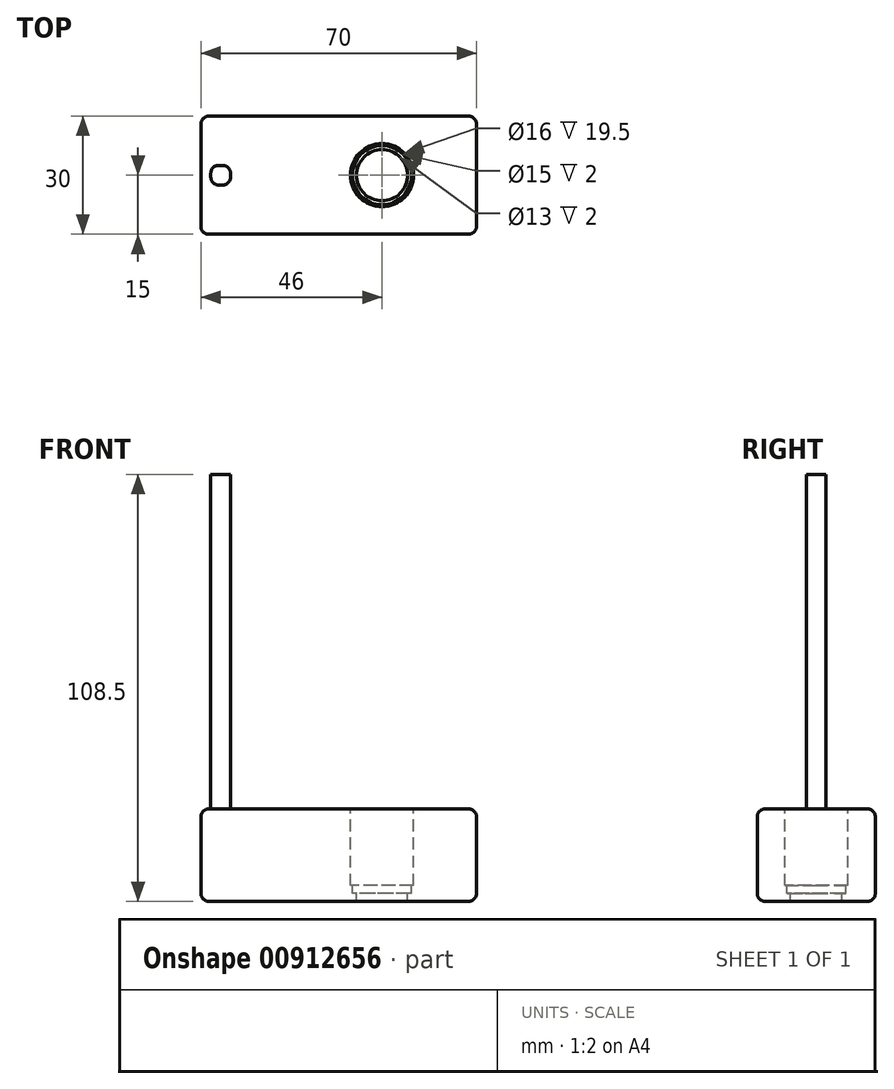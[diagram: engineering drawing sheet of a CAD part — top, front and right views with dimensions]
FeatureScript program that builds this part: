
annotation { "Feature Type Name" : "Feature", "Feature Type Description" : "" }
export const myFeature = defineFeature(function(context is Context, id is Id, definition is map)
    precondition{}
    {
        {
            var Q0;
            Q0=qCreatedBy(makeId("Front.planeOp"),FACE);
            var sketch = newSketch(context, id + "F0", { "sketchPlane" : qUnion([Q0])});
            skLineSegment(sketch, "E0.bottom", {"start": v(35, -11.75) * mm, "end": v(-35, -11.75) * mm});
            skLineSegment(sketch, "E0.top", {"start": v(35, 11.75) * mm, "end": v(-35, 11.75) * mm});
            skLineSegment(sketch, "E0.left", {"start": v(35, -11.75) * mm, "end": v(35, 11.75) * mm});
            skLineSegment(sketch, "E0.right", {"start": v(-35, -11.75) * mm, "end": v(-35, 11.75) * mm});
            skPoint(sketch, "E0.middle", {"position": v(0, 0) * mm});
            skSolve(sketch);
        }
        {
            var Q0;
            Q0=makeQuery(id+"F0.imprint","IMPRINT",FACE,{"disambiguationData":[TD([[makeQuery(id+"F0.imprint","IMPRINT",EDGE,{"derivedFrom":sQuery(id+"F0.wireOp",EDGE,"E0.bottom")}),-1.0]])]});
            extrude(context, id + "F1", {"entities" : qUnion([Q0]), "depth" : 30 * mm, "offsetDistance" : 25 * mm});
        }
        {
            var Q0;
            Q0=makeQuery(id+"F1.opExtrude","SWEPT_FACE",FACE,{"disambiguationData":[OSD([sQuery(id+"F0.wireOp",EDGE,"E0.top")])]});
            var sketch = newSketch(context, id + "F2", { "sketchPlane" : qUnion([Q0])});
            skLineSegment(sketch, "E1", {"start": v(35, -15) * mm, "end": v(11, -15) * mm, "construction": true});
            skCircle(sketch, "E2", {"center": v(11, -15) * mm, "radius": 8 * mm});
            skSolve(sketch);
        }
        {
            var Q0;
            Q0=makeQuery(id+"F2.imprint","IMPRINT",FACE,{"disambiguationData":[TD([[makeQuery(id+"F2.imprint","IMPRINT",EDGE,{"derivedFrom":sQuery(id+"F2.wireOp",EDGE,"E2")}),1.0]])]});
            extrude(context, id + "F3", {"entities" : qUnion([Q0]), "operationType" : NewBodyOperationType.REMOVE, "oppositeDirection" : true, "depth" : 19.5 * mm, "offsetDistance" : 25 * mm});
        }
        {
            var Q0;
            Q0=makeQuery(id+"F3.boolean.opBoolean","COPY",FACE,{"derivedFrom":makeQuery(id+"F3.opExtrude","CAP_FACE",FACE,{"disambiguationData":[OSD([sQuery(id+"F2.wireOp",EDGE,"E2")])],"isStart":false})});
            var sketch = newSketch(context, id + "F4", { "sketchPlane" : qUnion([Q0])});
            skCircle(sketch, "E3", {"center": v(11, -15) * mm, "radius": 7.5 * mm});
            skSolve(sketch);
        }
        {
            var Q0;
            Q0=makeQuery(id+"F4.imprint","IMPRINT",FACE,{"disambiguationData":[TD([[makeQuery(id+"F4.imprint","IMPRINT",EDGE,{"derivedFrom":sQuery(id+"F4.wireOp",EDGE,"E3")}),1.0]])]});
            extrude(context, id + "F5", {"entities" : qUnion([Q0]), "operationType" : NewBodyOperationType.REMOVE, "oppositeDirection" : true, "depth" : 2 * mm, "offsetDistance" : 25 * mm});
        }
        {
            var Q0;
            Q0=makeQuery(id+"F5.boolean.opBoolean","COPY",FACE,{"derivedFrom":makeQuery(id+"F5.opExtrude","CAP_FACE",FACE,{"disambiguationData":[OSD([sQuery(id+"F4.wireOp",EDGE,"E3")])],"isStart":false})});
            var sketch = newSketch(context, id + "F6", { "sketchPlane" : qUnion([Q0])});
            skCircle(sketch, "E4", {"center": v(11, -15) * mm, "radius": 6.5 * mm});
            skSolve(sketch);
        }
        {
            var Q0;
            Q0=makeQuery(id+"F6.imprint","IMPRINT",FACE,{"disambiguationData":[TD([[makeQuery(id+"F6.imprint","IMPRINT",EDGE,{"derivedFrom":sQuery(id+"F6.wireOp",EDGE,"E4")}),1.0]])]});
            extrude(context, id + "F7", {"entities" : qUnion([Q0]), "operationType" : NewBodyOperationType.REMOVE, "endBound" : BoundingType.THROUGH_ALL, "oppositeDirection" : true, "depth" : 25 * mm, "offsetDistance" : 25 * mm});
        }
        {
            var Q0;
            Q0=makeQuery(id+"F1.opExtrude","SWEPT_FACE",FACE,{"disambiguationData":[OSD([sQuery(id+"F0.wireOp",EDGE,"E0.top")])]});
            var sketch = newSketch(context, id + "F8", { "sketchPlane" : qUnion([Q0])});
            skLineSegment(sketch, "E5.bottom", {"start": v(-27.5, -17.5) * mm, "end": v(-32.5, -17.5) * mm});
            skLineSegment(sketch, "E5.top", {"start": v(-27.5, -12.5) * mm, "end": v(-32.5, -12.5) * mm});
            skLineSegment(sketch, "E5.left", {"start": v(-27.5, -17.5) * mm, "end": v(-27.5, -12.5) * mm});
            skLineSegment(sketch, "E5.right", {"start": v(-32.5, -17.5) * mm, "end": v(-32.5, -12.5) * mm});
            skPoint(sketch, "E5.middle", {"position": v(-30, -15) * mm});
            skSolve(sketch);
        }
        {
            var Q0;
            Q0=makeQuery(id+"F8.imprint","IMPRINT",FACE,{"disambiguationData":[TD([[makeQuery(id+"F8.imprint","IMPRINT",EDGE,{"derivedFrom":sQuery(id+"F8.wireOp",EDGE,"E5.bottom")}),-1.0]])]});
            extrude(context, id + "F9", {"entities" : qUnion([Q0]), "operationType" : NewBodyOperationType.ADD, "depth" : 85 * mm, "offsetDistance" : 25 * mm});
        }
        {
            var Q0;
            Q0=makeQuery(id+"F1.opExtrude","CAP_EDGE",EDGE,{"disambiguationData":[OSD([sQuery(id+"F0.wireOp",EDGE,"E0.top")])],"isStart":false});
            var Q1;
            Q1=makeQuery(id+"F1.opExtrude","SWEPT_EDGE",EDGE,{"disambiguationData":[OSD([sQuery(id+"F0.wireOp",EDGE,"E0.top"),sQuery(id+"F0.wireOp",EDGE,"E0.left")])]});
            var Q2;
            Q2=makeQuery(id+"F1.opExtrude","CAP_EDGE",EDGE,{"disambiguationData":[OSD([sQuery(id+"F0.wireOp",EDGE,"E0.left")])],"isStart":false});
            var Q3;
            Q3=makeQuery(id+"F1.opExtrude","CAP_EDGE",EDGE,{"disambiguationData":[OSD([sQuery(id+"F0.wireOp",EDGE,"E0.left")])],"isStart":true});
            var Q4;
            Q4=makeQuery(id+"F1.opExtrude","SWEPT_EDGE",EDGE,{"disambiguationData":[OSD([sQuery(id+"F0.wireOp",EDGE,"E0.bottom"),sQuery(id+"F0.wireOp",EDGE,"E0.left")])]});
            var Q5;
            Q5=makeQuery(id+"F1.opExtrude","CAP_EDGE",EDGE,{"disambiguationData":[OSD([sQuery(id+"F0.wireOp",EDGE,"E0.top")])],"isStart":true});
            var Q6;
            Q6=makeQuery(id+"F1.opExtrude","CAP_EDGE",EDGE,{"disambiguationData":[OSD([sQuery(id+"F0.wireOp",EDGE,"E0.bottom")])],"isStart":true});
            var Q7;
            Q7=makeQuery(id+"F1.opExtrude","CAP_EDGE",EDGE,{"disambiguationData":[OSD([sQuery(id+"F0.wireOp",EDGE,"E0.right")])],"isStart":true});
            var Q8;
            Q8=makeQuery(id+"F1.opExtrude","SWEPT_EDGE",EDGE,{"disambiguationData":[OSD([sQuery(id+"F0.wireOp",EDGE,"E0.top"),sQuery(id+"F0.wireOp",EDGE,"E0.right")])]});
            var Q9;
            Q9=makeQuery(id+"F1.opExtrude","CAP_EDGE",EDGE,{"disambiguationData":[OSD([sQuery(id+"F0.wireOp",EDGE,"E0.right")])],"isStart":false});
            var Q10;
            Q10=makeQuery(id+"F1.opExtrude","SWEPT_EDGE",EDGE,{"disambiguationData":[OSD([sQuery(id+"F0.wireOp",EDGE,"E0.bottom"),sQuery(id+"F0.wireOp",EDGE,"E0.right")])]});
            var Q11;
            Q11=makeQuery(id+"F1.opExtrude","CAP_EDGE",EDGE,{"disambiguationData":[OSD([sQuery(id+"F0.wireOp",EDGE,"E0.bottom")])],"isStart":false});
            var Q12;
            Q12=makeQuery(id+"F9.opExtrude","SWEPT_EDGE",EDGE,{"disambiguationData":[OSD([sQuery(id+"F8.wireOp",EDGE,"E5.bottom"),sQuery(id+"F8.wireOp",EDGE,"E5.right")])]});
            var Q13;
            Q13=makeQuery(id+"F9.opExtrude","SWEPT_EDGE",EDGE,{"disambiguationData":[OSD([sQuery(id+"F8.wireOp",EDGE,"E5.bottom"),sQuery(id+"F8.wireOp",EDGE,"E5.left")])]});
            var Q14;
            Q14=makeQuery(id+"F9.opExtrude","SWEPT_EDGE",EDGE,{"disambiguationData":[OSD([sQuery(id+"F8.wireOp",EDGE,"E5.top"),sQuery(id+"F8.wireOp",EDGE,"E5.left")])]});
            var Q15;
            Q15=makeQuery(id+"F9.opExtrude","SWEPT_EDGE",EDGE,{"disambiguationData":[OSD([sQuery(id+"F8.wireOp",EDGE,"E5.top"),sQuery(id+"F8.wireOp",EDGE,"E5.right")])]});
            fillet(context, id + "F10", {"entities" : qUnion([Q0, Q1, Q2, Q3, Q4, Q5, Q6, Q7, Q8, Q9, Q10, Q11, Q12, Q13, Q14, Q15]), "radius" : 2 * mm, "tangentPropagation" : true, "allowEdgeOverflow" : false});
        }
    });
